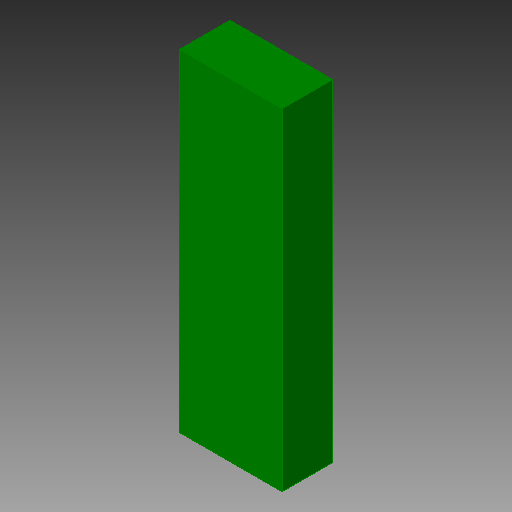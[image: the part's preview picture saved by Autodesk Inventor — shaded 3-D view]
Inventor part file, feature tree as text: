
AUTODESK INVENTOR PART (.ipt)
format: ipt  version: 2018 (Build 220112000, 112)  size: 80,384 bytes
history: native  units: in
note: dims shown in document units (in); Inventor stores cm internally (conversion verified against a paired STEP export)
features: other x1, extrude x1
ambient origin geometry x8: Origin, YZ Plane, XZ Plane, XY Plane, X Axis, Y Axis, Z Axis, Center Point
bodies: Solid1 (feature_tree)
feature tree (2):
  other  "MS3V-T1R, 32_768KHZ_91"
  extrude  "Extrusion1"  Depth=0.0394in TaperAngle=0.0deg
